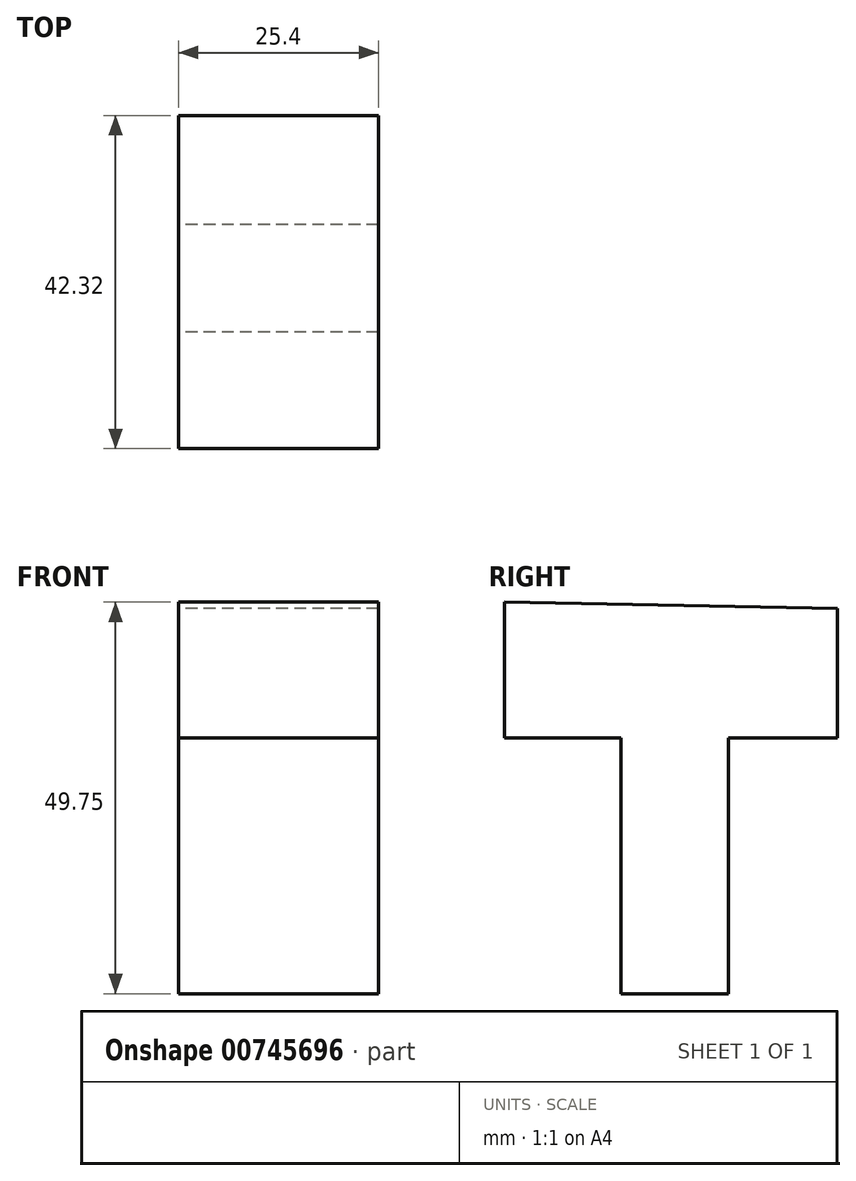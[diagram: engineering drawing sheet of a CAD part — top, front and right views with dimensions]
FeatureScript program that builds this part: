
annotation { "Feature Type Name" : "Feature", "Feature Type Description" : "" }
export const myFeature = defineFeature(function(context is Context, id is Id, definition is map)
    precondition{}
    {
        {
            var Q0;
            Q0=qCreatedBy(makeId("Right.planeOp"),FACE);
            var sketch = newSketch(context, id + "F0", { "sketchPlane" : qUnion([Q0])});
            skLineSegment(sketch, "E0", {"start": v(0, 49.75) * mm, "end": v(0, 32.47) * mm});
            skLineSegment(sketch, "E1", {"start": v(0, 32.47) * mm, "end": v(14.78, 32.47) * mm});
            skLineSegment(sketch, "E2", {"start": v(14.78, 32.47) * mm, "end": v(14.78, 0) * mm});
            skLineSegment(sketch, "E3", {"start": v(14.78, 0) * mm, "end": v(28.45, 0) * mm});
            skLineSegment(sketch, "E4", {"start": v(28.45, 0) * mm, "end": v(28.45, 32.47) * mm});
            skLineSegment(sketch, "E5", {"start": v(28.45, 32.47) * mm, "end": v(42.32, 32.47) * mm});
            skLineSegment(sketch, "E6", {"start": v(42.32, 32.47) * mm, "end": v(42.32, 48.95) * mm});
            skLineSegment(sketch, "E7", {"start": v(42.32, 48.95) * mm, "end": v(0, 49.75) * mm});
            skSolve(sketch);
        }
        {
            var Q0;
            Q0=makeQuery(id+"F0.imprint","IMPRINT",FACE,{"disambiguationData":[TD([[makeQuery(id+"F0.imprint","IMPRINT",EDGE,{"derivedFrom":sQuery(id+"F0.wireOp",EDGE,"E0")}),1.0]])]});
            extrude(context, id + "F1", {"entities" : qUnion([Q0]), "depth" : 25.4 * mm, "offsetDistance" : 25.4 * mm});
        }
    });
